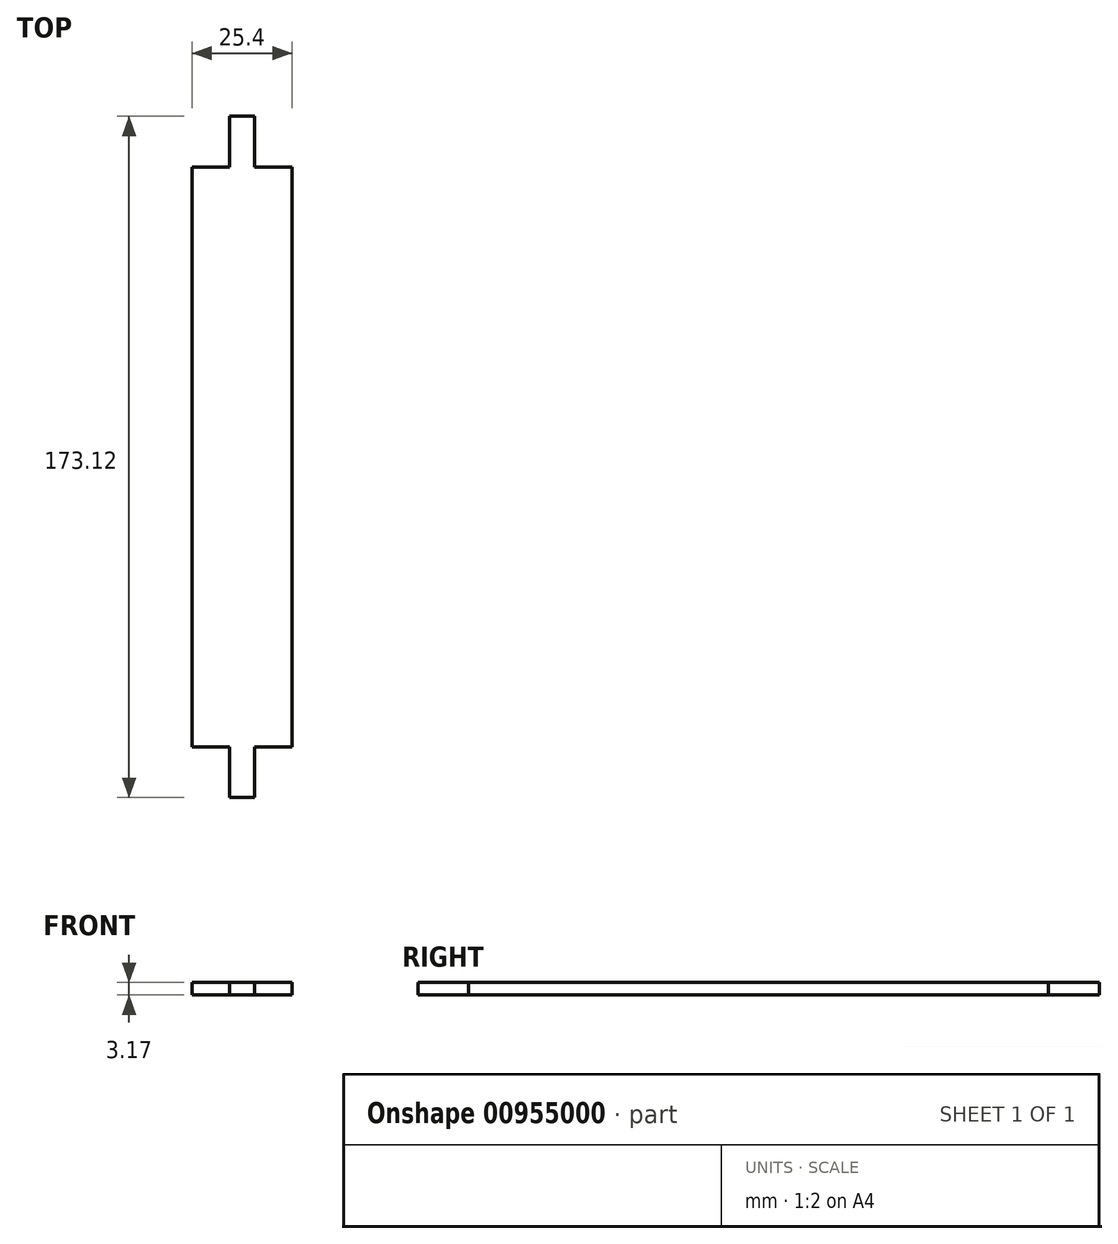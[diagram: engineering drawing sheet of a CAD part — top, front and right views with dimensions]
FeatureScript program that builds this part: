
annotation { "Feature Type Name" : "Feature", "Feature Type Description" : "" }
export const myFeature = defineFeature(function(context is Context, id is Id, definition is map)
    precondition{}
    {
        {
            var Q0;
            Q0=qCreatedBy(makeId("Top.planeOp"),FACE);
            var sketch = newSketch(context, id + "F0", { "sketchPlane" : qUnion([Q0])});
            skLineSegment(sketch, "E0", {"start": v(0, 0) * mm, "end": v(0, 86.56) * mm, "construction": true});
            skLineSegment(sketch, "E1", {"start": v(-12.7, 0) * mm, "end": v(-12.7, 73.66) * mm});
            skLineSegment(sketch, "E2", {"start": v(-12.7, 73.66) * mm, "end": v(-3.17, 73.66) * mm});
            skLineSegment(sketch, "E3", {"start": v(-3.17, 73.66) * mm, "end": v(-3.18, 86.56) * mm});
            skLineSegment(sketch, "E4", {"start": v(-3.18, 86.56) * mm, "end": v(3.18, 86.56) * mm});
            skLineSegment(sketch, "E5", {"start": v(3.17, 86.56) * mm, "end": v(3.18, 73.66) * mm});
            skLineSegment(sketch, "E6", {"start": v(3.17, 73.66) * mm, "end": v(12.7, 73.66) * mm});
            skLineSegment(sketch, "E7", {"start": v(12.7, 73.66) * mm, "end": v(12.7, 0) * mm});
            skLineSegment(sketch, "E8", {"start": v(-12.7, 0) * mm, "end": v(12.7, 0) * mm, "construction": true});
            skPoint(sketch, "E9", {"position": v(0, 0) * mm});
            skPoint(sketch, "E10", {"position": v(0, 86.56) * mm});
            skLineSegment(sketch, "E11.MirrorCS", {"start": v(-3.18, -86.56) * mm, "end": v(3.18, -86.56) * mm});
            skLineSegment(sketch, "E12.MirrorCS", {"start": v(-12.7, -73.66) * mm, "end": v(-3.17, -73.66) * mm});
            skLineSegment(sketch, "E13.MirrorCS", {"start": v(3.17, -73.66) * mm, "end": v(12.7, -73.66) * mm});
            skLineSegment(sketch, "E14.MirrorCS", {"start": v(3.17, -86.56) * mm, "end": v(3.18, -73.66) * mm});
            skLineSegment(sketch, "E15.MirrorCS", {"start": v(-3.17, -73.66) * mm, "end": v(-3.18, -86.56) * mm});
            skLineSegment(sketch, "E16.MirrorCS", {"start": v(12.7, -73.66) * mm, "end": v(12.7, 0) * mm});
            skLineSegment(sketch, "E17.MirrorCS", {"start": v(0, 0) * mm, "end": v(0, -86.56) * mm, "construction": true});
            skLineSegment(sketch, "E18.MirrorCS", {"start": v(-12.7, 0) * mm, "end": v(-12.7, -73.66) * mm});
            skPoint(sketch, "E19.MirrorP", {"position": v(0, -86.56) * mm});
            skSolve(sketch);
        }
        {
            var Q0;
            Q0 = qSketchRegion(id + "F0", true);
            extrude(context, id + "F1", {"entities" : qUnion([Q0]), "depth" : 3.17 * mm, "offsetDistance" : 25.4 * mm});
        }
    });
